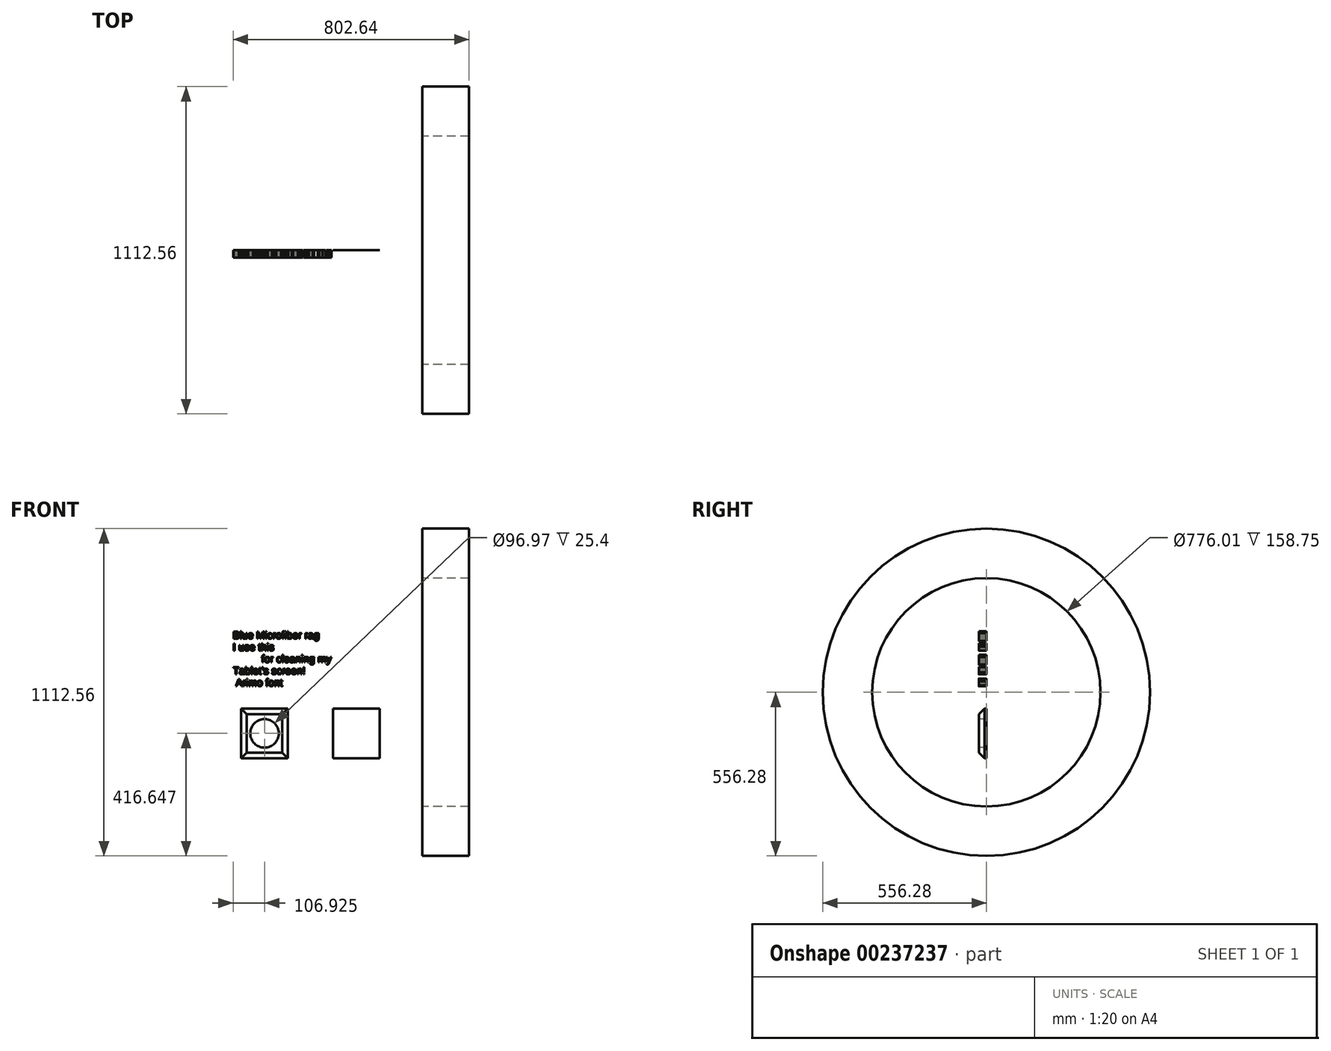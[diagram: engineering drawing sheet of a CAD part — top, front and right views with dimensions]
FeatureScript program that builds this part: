
annotation { "Feature Type Name" : "Feature", "Feature Type Description" : "" }
export const myFeature = defineFeature(function(context is Context, id is Id, definition is map)
    precondition{}
    {
        {
            var Q0;
            Q0=qCreatedBy(makeId("Front.planeOp"),FACE);
            var sketch = newSketch(context, id + "F4", { "sketchPlane" : qUnion([Q0])});
            skLineSegment(sketch, "E0.bottom", {"start": v(0, 0) * mm, "end": v(158.75, 0) * mm});
            skLineSegment(sketch, "E0.top", {"start": v(0, 168.28) * mm, "end": v(158.75, 168.28) * mm});
            skLineSegment(sketch, "E0.left", {"start": v(0, 0) * mm, "end": v(0, 168.28) * mm});
            skLineSegment(sketch, "E0.right", {"start": v(158.75, 0) * mm, "end": v(158.75, 168.28) * mm});
            skText(sketch, "E1", { "text": "Blue Microfiber rag\nI use this\n          for cleaning my \nTablet\'s screen!\n Arimo font", "fontName": "Arimo-Regular.ttf"});
            const initialGuessFAa53rOV7FdX9qIsT_0  = {"E1": [-0.02834, 0.40602, 1, 0, 0.02525]};
            skSetInitialGuess(sketch, initialGuessFAa53rOV7FdX9qIsT_0);
            skSolve(sketch);
        }
        {
            var Q0;
            Q0 = qSketchRegion(id + "F4", true);
            extrude(context, id + "F5", {"entities" : qUnion([Q0]), "depth" : 25.4 * mm});
        }
        {
            var Q0;
            Q0=qCreatedBy(makeId("Front.planeOp"),FACE);
            var sketch = newSketch(context, id + "F0", { "sketchPlane" : qUnion([Q0])});
            skLineSegment(sketch, "E2.bottom", {"start": v(311.84, 0) * mm, "end": v(470.59, 0) * mm});
            skLineSegment(sketch, "E2.top", {"start": v(311.84, 168.28) * mm, "end": v(470.59, 168.28) * mm});
            skLineSegment(sketch, "E2.left", {"start": v(311.84, 0) * mm, "end": v(311.84, 168.28) * mm});
            skLineSegment(sketch, "E2.right", {"start": v(470.59, 0) * mm, "end": v(470.59, 168.28) * mm});
            skSolve(sketch);
        }
        {
            var Q0;
            Q0=makeQuery(id+"F0.imprint","IMPRINT",FACE,{"disambiguationData":[TD([[makeQuery(id+"F0.imprint","IMPRINT",EDGE,{"derivedFrom":sQuery(id+"F0.wireOp",EDGE,"E2.bottom")}),1.0]])]});
            extrude(context, id + "F1", {"entities" : qUnion([Q0]), "depth" : 3 / 3251.2 * mm});
        }
        {
            var Q0;
            Q0=makeQuery(id+"F5.opExtrude","CAP_EDGE",EDGE,{"disambiguationData":[OSD([sQuery(id+"F4.wireOp",EDGE,"E0.right")])],"isStart":false});
            var Q1;
            Q1=makeQuery(id+"F5.opExtrude","CAP_EDGE",EDGE,{"disambiguationData":[OSD([sQuery(id+"F4.wireOp",EDGE,"E0.bottom")])],"isStart":false});
            var Q2;
            Q2=makeQuery(id+"F5.opExtrude","CAP_EDGE",EDGE,{"disambiguationData":[OSD([sQuery(id+"F4.wireOp",EDGE,"E0.left")])],"isStart":false});
            var Q3;
            Q3=makeQuery(id+"F5.opExtrude","CAP_EDGE",EDGE,{"disambiguationData":[OSD([sQuery(id+"F4.wireOp",EDGE,"E0.top")])],"isStart":false});
            chamfer(context, id + "F6", {"entities" : qUnion([Q0, Q1, Q2, Q3]), "width" : 19.05 * mm, "tangentPropagation" : true});
        }
        {
            var Q0;
            Q0=makeQuery(id+"F5.opExtrude","CAP_FACE",FACE,{"disambiguationData":[OSD([sQuery(id+"F4.wireOp",EDGE,"E0.bottom"),sQuery(id+"F4.wireOp",EDGE,"E0.top"),sQuery(id+"F4.wireOp",EDGE,"E0.left"),sQuery(id+"F4.wireOp",EDGE,"E0.right")])],"isStart":false});
            var sketch = newSketch(context, id + "F2", { "sketchPlane" : qUnion([Q0])});
            skLineSegment(sketch, "E3", {"start": v(19.05, 149.23) * mm, "end": v(139.7, 19.05) * mm, "construction": true});
            skLineSegment(sketch, "E4", {"start": v(139.7, 149.22) * mm, "end": v(19.05, 19.05) * mm, "construction": true});
            skCircle(sketch, "E5", {"center": v(79.37, 84.14) * mm, "radius": 51.74 * mm, "construction": true});
            skPoint(sketch, "E5.centerSnap0", {"position": v(79.37, 84.14) * mm});
            skCircle(sketch, "E6", {"center": v(79.37, 84.14) * mm, "radius": 48.48 * mm});
            skSolve(sketch);
        }
        {
            var Q0;
            Q0=makeQuery(id+"F2.imprint","IMPRINT",FACE,{"disambiguationData":[TD([[makeQuery(id+"F2.imprint","IMPRINT",EDGE,{"derivedFrom":sQuery(id+"F2.wireOp",EDGE,"E6")}),1.0]])]});
            extrude(context, id + "F7", {"entities" : qUnion([Q0]), "operationType" : NewBodyOperationType.REMOVE, "oppositeDirection" : true, "depth" : 25.4 * mm});
        }
        {
            var Q0;
            Q0=qCreatedBy(makeId("Front.planeOp"),FACE);
            var sketch = newSketch(context, id + "F3", { "sketchPlane" : qUnion([Q0])});
            skLineSegment(sketch, "E7.bottom", {"start": v(775.1, 780.05) * mm, "end": v(616.34, 780.05) * mm});
            skLineSegment(sketch, "E7.top", {"start": v(775.1, 611.78) * mm, "end": v(616.34, 611.78) * mm});
            skLineSegment(sketch, "E7.left", {"start": v(775.1, 780.05) * mm, "end": v(775.1, 611.78) * mm});
            skLineSegment(sketch, "E7.right", {"start": v(616.34, 780.05) * mm, "end": v(616.34, 611.78) * mm});
            skPoint(sketch, "E7.middle", {"position": v(695.72, 695.91) * mm});
            skLineSegment(sketch, "E8", {"start": v(540.18, 223.77) * mm, "end": v(905.7, 223.77) * mm, "construction": true});
            skSolve(sketch);
        }
        {
            var Q0;
            Q0 = qSketchRegion(id + "F3", true);
            var Q1;
            Q1=sQuery(id+"F3.wireOp",EDGE,"E8");
            revolve(context, id + "F8", {"entities" : qUnion([Q0]), "axis" : qUnion([Q1]), "revolveType" : RevolveType.FULL});
        }
    });
